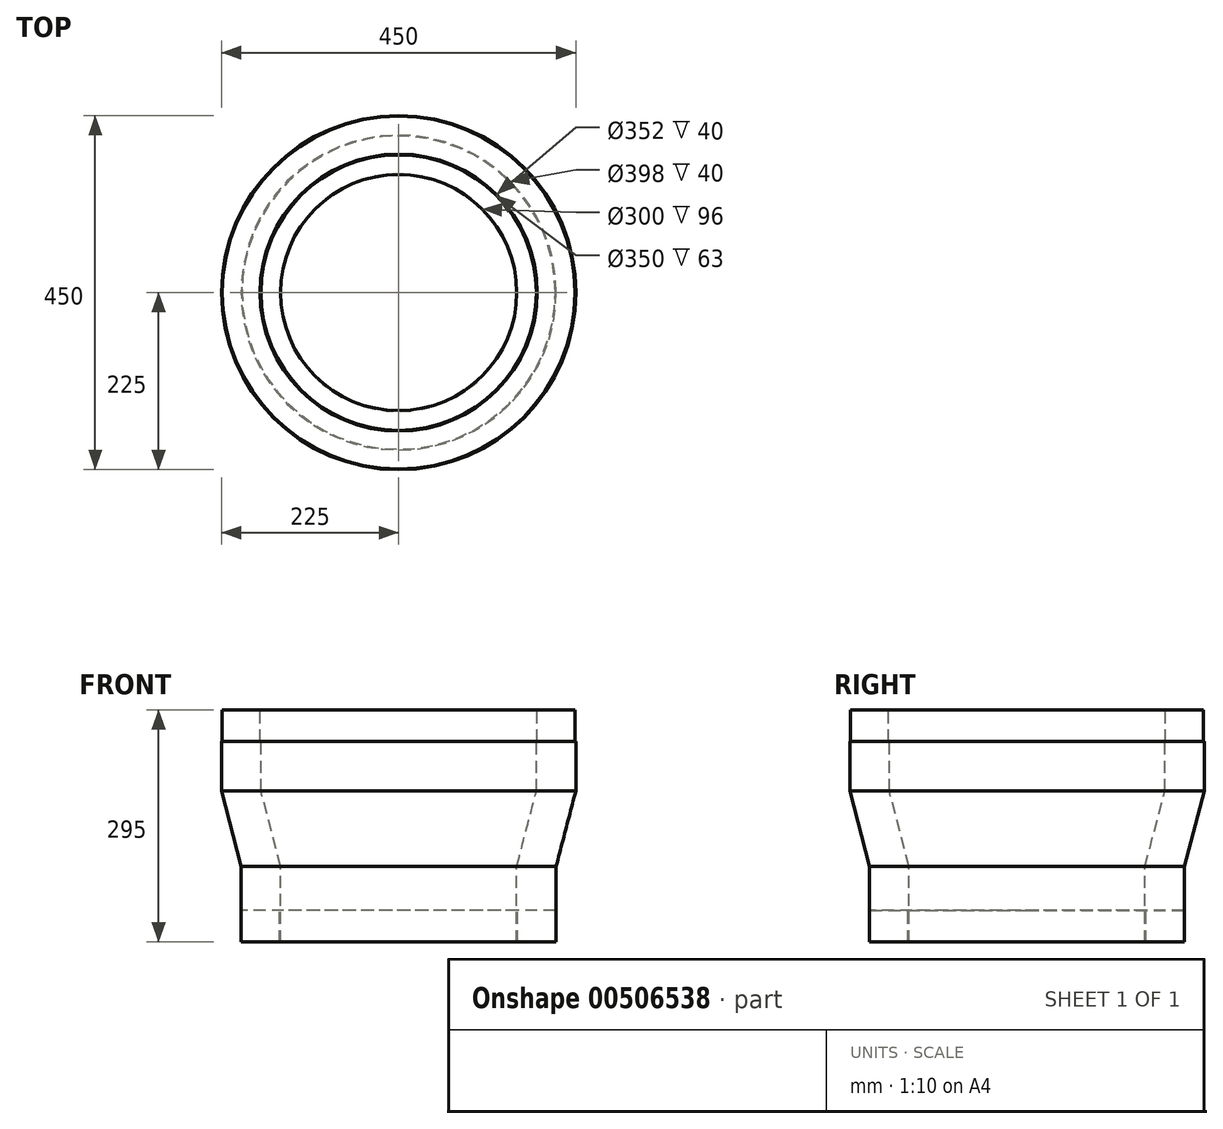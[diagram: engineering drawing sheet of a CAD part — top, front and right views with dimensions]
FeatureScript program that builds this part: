
annotation { "Feature Type Name" : "Feature", "Feature Type Description" : "" }
export const myFeature = defineFeature(function(context is Context, id is Id, definition is map)
    precondition{}
    {
        {
            var Q0;
            Q0=qCreatedBy(makeId("Front.planeOp"),FACE);
            var sketch = newSketch(context, id + "F0", { "sketchPlane" : qUnion([Q0])});
            skLineSegment(sketch, "E0", {"start": v(0, 433.08) * mm, "end": v(0, -434.74) * mm, "construction": true});
            skLineSegment(sketch, "E1", {"start": v(-150, -254.87) * mm, "end": v(-150, -158.87) * mm});
            skLineSegment(sketch, "E2", {"start": v(-150, -254.87) * mm, "end": v(-151, -254.87) * mm});
            skLineSegment(sketch, "E3", {"start": v(-151, -254.87) * mm, "end": v(-151, -214.87) * mm});
            skLineSegment(sketch, "E4", {"start": v(-151, -214.87) * mm, "end": v(-199, -214.87) * mm});
            skLineSegment(sketch, "E5", {"start": v(-199, -214.87) * mm, "end": v(-199, -254.87) * mm});
            skLineSegment(sketch, "E6", {"start": v(-199, -254.87) * mm, "end": v(-200, -254.87) * mm});
            skLineSegment(sketch, "E7", {"start": v(-200, -254.87) * mm, "end": v(-200, -158.87) * mm});
            skLineSegment(sketch, "E8", {"start": v(-224, 40.13) * mm, "end": v(-176, 40.13) * mm});
            skLineSegment(sketch, "E9", {"start": v(-176, 40.13) * mm, "end": v(-176, 0.13) * mm});
            skLineSegment(sketch, "E10", {"start": v(-176, 0.13) * mm, "end": v(-175, 0.13) * mm});
            skLineSegment(sketch, "E11", {"start": v(-175, 0.13) * mm, "end": v(-175, -62.87) * mm});
            skLineSegment(sketch, "E12", {"start": v(-224, 40.13) * mm, "end": v(-224, 0.13) * mm});
            skLineSegment(sketch, "E13", {"start": v(-224, 0.13) * mm, "end": v(-225, 0.13) * mm});
            skLineSegment(sketch, "E14", {"start": v(-225, 0.13) * mm, "end": v(-225, -62.87) * mm});
            skLineSegment(sketch, "E15", {"start": v(-175, -62.87) * mm, "end": v(-150, -158.87) * mm});
            skLineSegment(sketch, "E16", {"start": v(-225, -62.87) * mm, "end": v(-200, -158.87) * mm});
            skSolve(sketch);
        }
        {
            var Q0;
            Q0=qSketchRegion(id+"F0",true);
            var Q1;
            Q1=sQuery(id+"F0.wireOp",EDGE,"E0");
            revolve(context, id + "F1", {"entities" : qUnion([Q0]), "axis" : qUnion([Q1]), "revolveType" : RevolveType.FULL});
        }
    });
